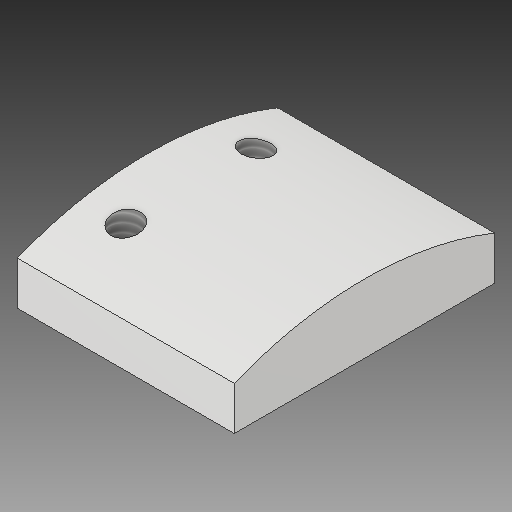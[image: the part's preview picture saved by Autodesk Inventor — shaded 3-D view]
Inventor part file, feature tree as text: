
AUTODESK INVENTOR PART (.ipt)
format: ipt  version: 2017 (Build 210142000, 142)  size: 120,320 bytes
history: native  units: in
note: dims shown in document units (in); Inventor stores cm internally (conversion verified against a paired STEP export)
features: sketch x2, extrude x1, hole x1, projected_geometry x1
ambient origin geometry x8: Origin, YZ Plane, XZ Plane, XY Plane, X Axis, Y Axis, Z Axis, Center Point
bodies: Solid1 (feature_tree)
feature tree (5):
  extrude  "Extrusion1"  Depth=0.125in
  hole  "Hole1"  [1 undecoded]
  sketch  "Sketch1"  dims[d0=0.75in d4=0.125in]
  sketch  "Sketch2"  dims[d6=1.0in d7=0.75in d8=0.625in d9=0.0in d10=0.625in d13=0.375in d14=0.75in d15=0.1875in d16=0.085in d17=0.224in d18=0.375in d19=0.25in d20=0.5635in d21=0.25in d22=0.8108in d23=0.125in d24=0.125in d25=0.125in]
  projected_geometry  "Projected Loop1"
note: 1 required parameter value undecoded (feature->parameter linkage not recoverable at this tier; creation-order binding heuristic only, values carry confidence <= 0.55)
